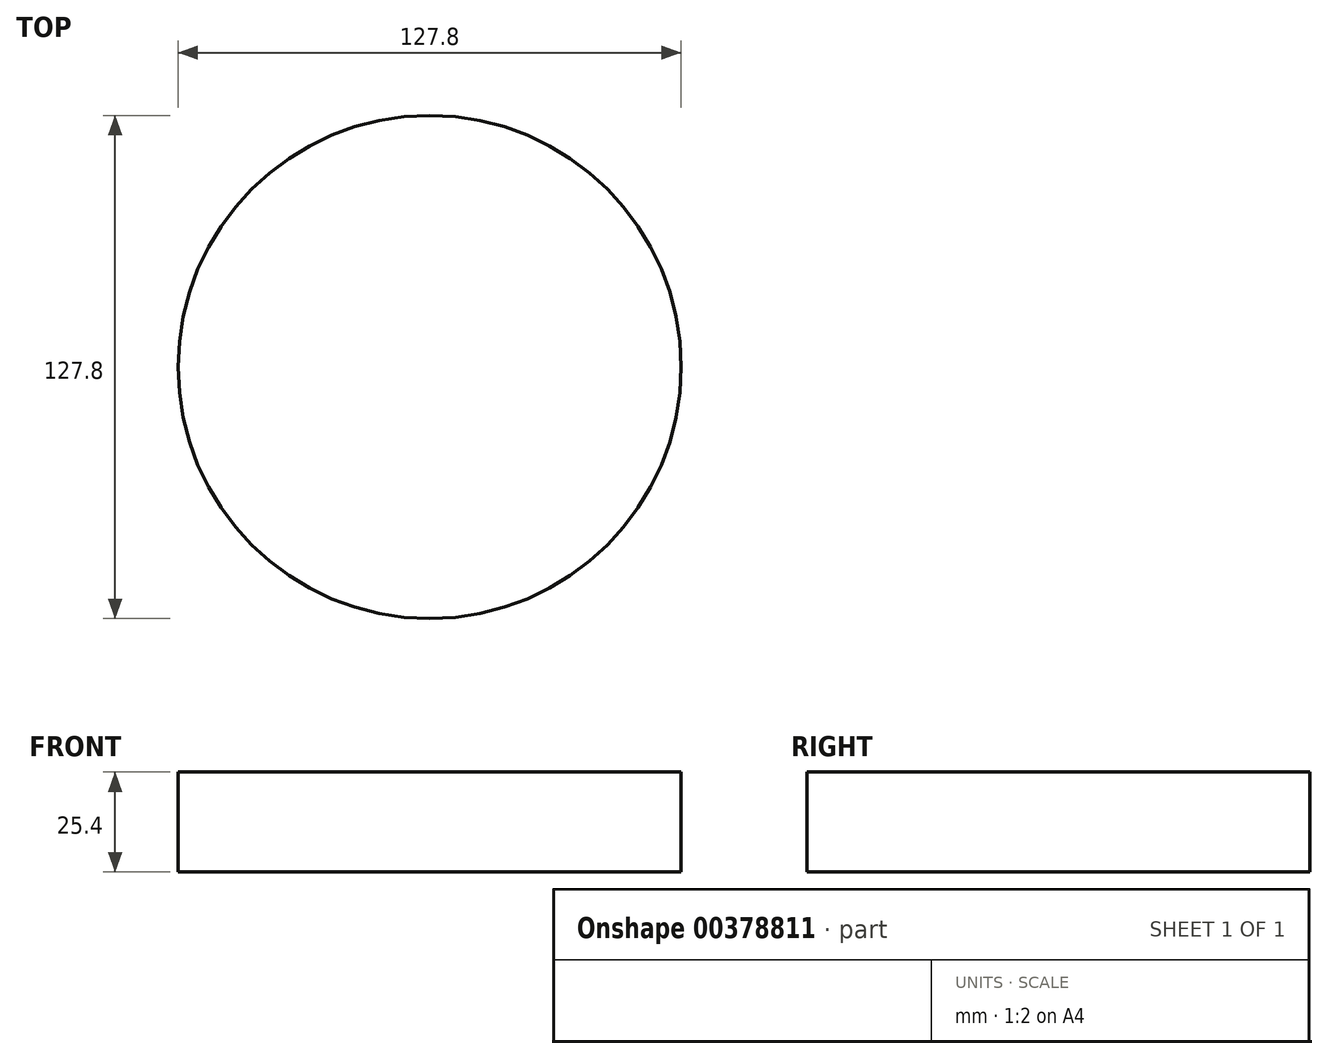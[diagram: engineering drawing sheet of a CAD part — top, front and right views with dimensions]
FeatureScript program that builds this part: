
annotation { "Feature Type Name" : "Feature", "Feature Type Description" : "" }
export const myFeature = defineFeature(function(context is Context, id is Id, definition is map)
    precondition{}
    {
        {
            assignVariable(context, id + "F0", {"name" : "baseHeight", "anyValue" : 25.4 * mm});
        }
        {
            var Q0;
            Q0=qCreatedBy(makeId("Top.planeOp"),FACE);
            var sketch = newSketch(context, id + "F1", { "sketchPlane" : qUnion([Q0])});
            skCircle(sketch, "E0", {"center": v(0, 0) * mm, "radius": 63.9 * mm});
            skSolve(sketch);
        }
        {
            var Q0;
            Q0=makeQuery(id+"F1.imprint","IMPRINT",FACE,{"disambiguationData":[TD([[makeQuery(id+"F1.imprint","IMPRINT",EDGE,{"derivedFrom":sQuery(id+"F1.wireOp",EDGE,"E0")}),1.0]])]});
            extrude(context, id + "F2", {"entities" : qUnion([Q0]), "depth" : getVariable(context, 'baseHeight')});
        }
    });
